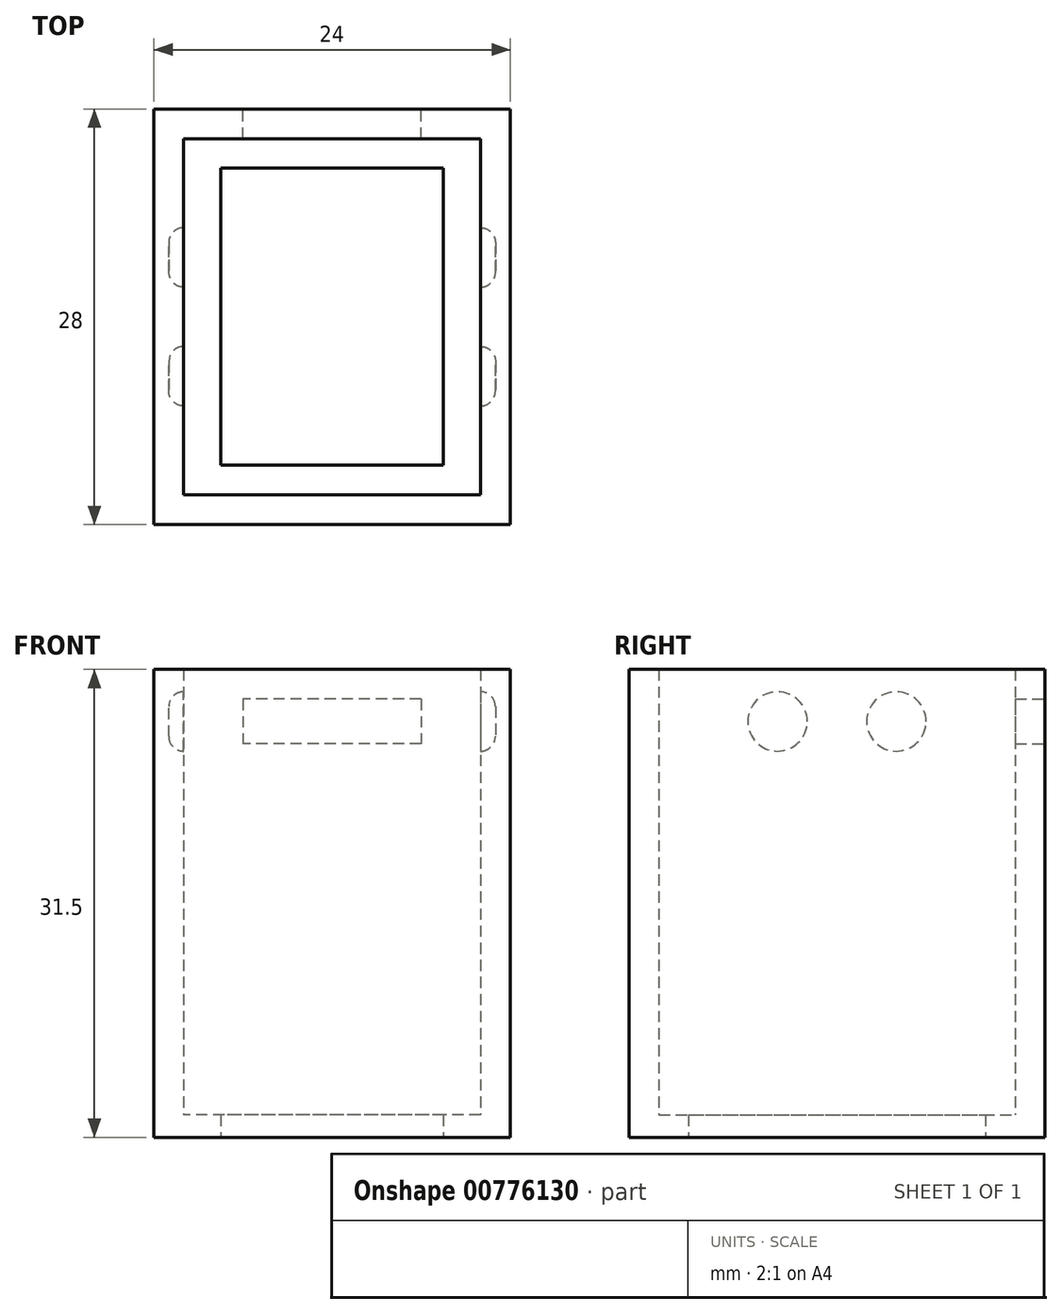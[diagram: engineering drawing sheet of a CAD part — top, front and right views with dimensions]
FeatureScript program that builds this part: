
annotation { "Feature Type Name" : "Feature", "Feature Type Description" : "" }
export const myFeature = defineFeature(function(context is Context, id is Id, definition is map)
    precondition{}
    {
        {
            var Q0;
            Q0=qCreatedBy(makeId("Top.planeOp"),FACE);
            var sketch = newSketch(context, id + "F0", { "sketchPlane" : qUnion([Q0])});
            skLineSegment(sketch, "E0.bottom", {"start": v(7.5, -10) * mm, "end": v(-7.5, -10) * mm});
            skLineSegment(sketch, "E0.top", {"start": v(7.5, 10) * mm, "end": v(-7.5, 10) * mm});
            skLineSegment(sketch, "E0.left", {"start": v(7.5, -10) * mm, "end": v(7.5, 10) * mm});
            skLineSegment(sketch, "E0.right", {"start": v(-7.5, -10) * mm, "end": v(-7.5, 10) * mm});
            skPoint(sketch, "E0.middle", {"position": v(0, 0) * mm});
            skLineSegment(sketch, "E1.bottom", {"start": v(12, -14) * mm, "end": v(-12, -14) * mm});
            skLineSegment(sketch, "E1.top", {"start": v(12, 14) * mm, "end": v(-12, 14) * mm});
            skLineSegment(sketch, "E1.left", {"start": v(12, -14) * mm, "end": v(12, 14) * mm});
            skLineSegment(sketch, "E1.right", {"start": v(-12, -14) * mm, "end": v(-12, 14) * mm});
            skSolve(sketch);
        }
        {
            var Q0;
            Q0=makeQuery(id+"F0.imprint","IMPRINT",FACE,{"disambiguationData":[TD([[makeQuery(id+"F0.imprint","IMPRINT",EDGE,{"derivedFrom":sQuery(id+"F0.wireOp",EDGE,"E0.bottom")}),1.0]])]});
            extrude(context, id + "F1", {"entities" : qUnion([Q0]), "depth" : 1.5 * mm, "offsetDistance" : 25 * mm});
        }
        {
            var Q0;
            Q0=makeQuery(id+"F1.opExtrude","CAP_FACE",FACE,{"disambiguationData":[OSD([sQuery(id+"F0.wireOp",EDGE,"E0.bottom"),sQuery(id+"F0.wireOp",EDGE,"E0.top"),sQuery(id+"F0.wireOp",EDGE,"E0.left"),sQuery(id+"F0.wireOp",EDGE,"E0.right"),sQuery(id+"F0.wireOp",EDGE,"E1.bottom"),sQuery(id+"F0.wireOp",EDGE,"E1.top"),sQuery(id+"F0.wireOp",EDGE,"E1.left"),sQuery(id+"F0.wireOp",EDGE,"E1.right")])],"isStart":false});
            var sketch = newSketch(context, id + "F2", { "sketchPlane" : qUnion([Q0])});
            skLineSegment(sketch, "E2.bottom", {"start": v(12, -14) * mm, "end": v(-12, -14) * mm});
            skLineSegment(sketch, "E2.top", {"start": v(12, 14) * mm, "end": v(-12, 14) * mm});
            skLineSegment(sketch, "E2.left", {"start": v(12, -14) * mm, "end": v(12, 14) * mm});
            skLineSegment(sketch, "E2.right", {"start": v(-12, -14) * mm, "end": v(-12, 14) * mm});
            skPoint(sketch, "E2.middle", {"position": v(0, 0) * mm});
            skLineSegment(sketch, "E3.bottom", {"start": v(10, -12) * mm, "end": v(-10, -12) * mm});
            skLineSegment(sketch, "E3.top", {"start": v(10, 12) * mm, "end": v(-10, 12) * mm});
            skLineSegment(sketch, "E3.left", {"start": v(10, -12) * mm, "end": v(10, 12) * mm});
            skLineSegment(sketch, "E3.right", {"start": v(-10, -12) * mm, "end": v(-10, 12) * mm});
            skSolve(sketch);
        }
        {
            var Q0;
            Q0 = qSketchRegion(id + "F2", true);
            extrude(context, id + "F3", {"entities" : qUnion([Q0]), "operationType" : NewBodyOperationType.ADD, "depth" : 30 * mm, "offsetDistance" : 25 * mm});
        }
        {
            var Q0;
            Q0=makeQuery(id+"F3.opExtrude","SWEPT_FACE",FACE,{"disambiguationData":[OSD([sQuery(id+"F2.wireOp",EDGE,"E3.right")])]});
            var sketch = newSketch(context, id + "F4", { "sketchPlane" : qUnion([Q0])});
            skPoint(sketch, "E4", {"position": v(0, 31.5) * mm});
            skPoint(sketch, "E5", {"position": v(0, 28) * mm});
            skPoint(sketch, "E6", {"position": v(4, 28) * mm});
            skPoint(sketch, "E7", {"position": v(-4, 28) * mm});
            skCircle(sketch, "E8", {"center": v(4, 28) * mm, "radius": 2 * mm});
            skCircle(sketch, "E9", {"center": v(-4, 28) * mm, "radius": 2 * mm});
            skSolve(sketch);
        }
        {
            var Q0;
            Q0=makeQuery(id+"F4.imprint","IMPRINT",FACE,{"disambiguationData":[TD([[makeQuery(id+"F4.imprint","IMPRINT",EDGE,{"derivedFrom":sQuery(id+"F4.wireOp",EDGE,"E9")}),1.0]])]});
            var Q1;
            Q1=makeQuery(id+"F4.imprint","IMPRINT",FACE,{"disambiguationData":[TD([[makeQuery(id+"F4.imprint","IMPRINT",EDGE,{"derivedFrom":sQuery(id+"F4.wireOp",EDGE,"E8")}),1.0]])]});
            extrude(context, id + "F5", {"entities" : qUnion([Q0, Q1]), "operationType" : NewBodyOperationType.REMOVE, "oppositeDirection" : true, "depth" : 1 * mm, "offsetDistance" : 25 * mm});
        }
        {
            var Q0;
            Q0=makeQuery(id+"F3.opExtrude","SWEPT_FACE",FACE,{"disambiguationData":[OSD([sQuery(id+"F2.wireOp",EDGE,"E3.left")])]});
            var sketch = newSketch(context, id + "F6", { "sketchPlane" : qUnion([Q0])});
            skPoint(sketch, "E10", {"position": v(0, 28) * mm});
            skPoint(sketch, "E10.positionSnap0", {"position": v(0, 31.5) * mm});
            skPoint(sketch, "E11", {"position": v(-4, 28) * mm});
            skPoint(sketch, "E12", {"position": v(4, 28) * mm});
            skCircle(sketch, "E13", {"center": v(-4, 28) * mm, "radius": 2 * mm});
            skCircle(sketch, "E14", {"center": v(4, 28) * mm, "radius": 2 * mm});
            skSolve(sketch);
        }
        {
            var Q0;
            Q0=makeQuery(id+"F6.imprint","IMPRINT",FACE,{"disambiguationData":[TD([[makeQuery(id+"F6.imprint","IMPRINT",EDGE,{"derivedFrom":sQuery(id+"F6.wireOp",EDGE,"E14")}),1.0]])]});
            var Q1;
            Q1=makeQuery(id+"F6.imprint","IMPRINT",FACE,{"disambiguationData":[TD([[makeQuery(id+"F6.imprint","IMPRINT",EDGE,{"derivedFrom":sQuery(id+"F6.wireOp",EDGE,"E13")}),1.0]])]});
            extrude(context, id + "F7", {"entities" : qUnion([Q0, Q1]), "operationType" : NewBodyOperationType.REMOVE, "oppositeDirection" : true, "depth" : 1 * mm, "offsetDistance" : 25 * mm});
        }
        {
            var Q0;
            Q0=makeQuery(id+"F7.boolean.opBoolean","COPY",EDGE,{"derivedFrom":makeQuery(id+"F7.opExtrude","CAP_EDGE",EDGE,{"disambiguationData":[OSD([sQuery(id+"F6.wireOp",EDGE,"E14")])],"isStart":false})});
            var Q1;
            Q1=makeQuery(id+"F7.boolean.opBoolean","COPY",EDGE,{"derivedFrom":makeQuery(id+"F7.opExtrude","CAP_EDGE",EDGE,{"disambiguationData":[OSD([sQuery(id+"F6.wireOp",EDGE,"E13")])],"isStart":false})});
            var Q2;
            Q2=makeQuery(id+"F5.boolean.opBoolean","COPY",EDGE,{"derivedFrom":makeQuery(id+"F5.opExtrude","CAP_EDGE",EDGE,{"disambiguationData":[OSD([sQuery(id+"F4.wireOp",EDGE,"E9")])],"isStart":false})});
            var Q3;
            Q3=makeQuery(id+"F5.boolean.opBoolean","COPY",EDGE,{"derivedFrom":makeQuery(id+"F5.opExtrude","CAP_EDGE",EDGE,{"disambiguationData":[OSD([sQuery(id+"F4.wireOp",EDGE,"E8")])],"isStart":false})});
            fillet(context, id + "F8", {"entities" : qUnion([Q0, Q1, Q2, Q3]), "radius" : 1 * mm, "allowEdgeOverflow" : false});
        }
        {
            var Q0;
            Q0=makeQuery(id+"F3.boolean.opBoolean","MERGE",FACE,{"derivedFrom":[makeQuery(id+"F1.opExtrude","SWEPT_FACE",FACE,{"disambiguationData":[OSD([sQuery(id+"F0.wireOp",EDGE,"E1.top")])]}),makeQuery(id+"F3.opExtrude","SWEPT_FACE",FACE,{"disambiguationData":[OSD([sQuery(id+"F2.wireOp",EDGE,"E2.top")])]})]});
            var sketch = newSketch(context, id + "F9", { "sketchPlane" : qUnion([Q0])});
            skLineSegment(sketch, "E15.bottom", {"start": v(-6, 29.5) * mm, "end": v(6, 29.5) * mm});
            skLineSegment(sketch, "E15.top", {"start": v(-6, 26.5) * mm, "end": v(6, 26.5) * mm});
            skLineSegment(sketch, "E15.left", {"start": v(-6, 29.5) * mm, "end": v(-6, 26.5) * mm});
            skLineSegment(sketch, "E15.right", {"start": v(6, 29.5) * mm, "end": v(6, 26.5) * mm});
            skPoint(sketch, "E15.middle", {"position": v(0, 28) * mm});
            skPoint(sketch, "E15.middle.positionSnap0", {"position": v(0, 31.5) * mm});
            skPoint(sketch, "E15.centerSnap0", {"position": v(0, 31.5) * mm});
            skSolve(sketch);
        }
        {
            var Q0;
            Q0=makeQuery(id+"F9.imprint","IMPRINT",FACE,{"disambiguationData":[TD([[makeQuery(id+"F9.imprint","IMPRINT",EDGE,{"derivedFrom":sQuery(id+"F9.wireOp",EDGE,"E15.bottom")}),-1.0]])]});
            extrude(context, id + "F10", {"entities" : qUnion([Q0]), "operationType" : NewBodyOperationType.REMOVE, "endBound" : BoundingType.UP_TO_NEXT, "oppositeDirection" : true, "depth" : 30 * mm, "offsetDistance" : 25 * mm});
        }
    });
